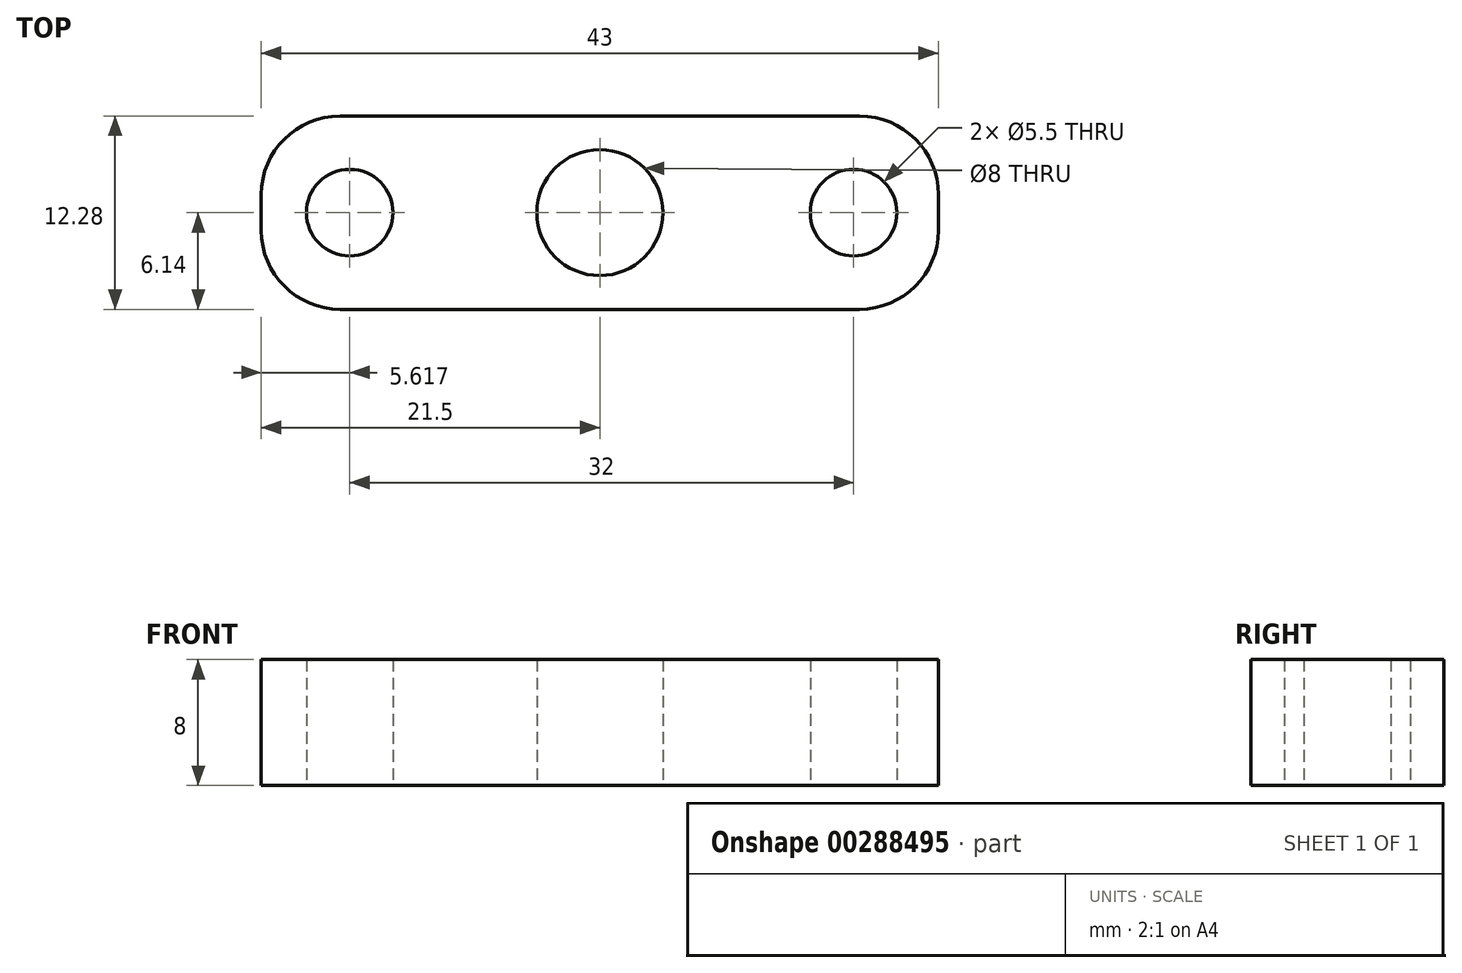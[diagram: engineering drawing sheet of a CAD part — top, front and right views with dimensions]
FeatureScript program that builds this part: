
annotation { "Feature Type Name" : "Feature", "Feature Type Description" : "" }
export const myFeature = defineFeature(function(context is Context, id is Id, definition is map)
    precondition{}
    {
        {
            var Q0;
            Q0=qCreatedBy(makeId("Top.planeOp"),FACE);
            var sketch = newSketch(context, id + "F0", { "sketchPlane" : qUnion([Q0])});
            skLineSegment(sketch, "E0.bottom", {"start": v(16.5, -6.14) * mm, "end": v(-16.5, -6.14) * mm});
            skLineSegment(sketch, "E0.top", {"start": v(16.5, 6.14) * mm, "end": v(-16.5, 6.14) * mm});
            skLineSegment(sketch, "E0.left", {"start": v(21.5, -1.14) * mm, "end": v(21.5, 1.14) * mm});
            skLineSegment(sketch, "E0.right", {"start": v(-21.5, -1.14) * mm, "end": v(-21.5, 1.14) * mm});
            skPoint(sketch, "E0.middle", {"position": v(0, 0) * mm});
            skCircle(sketch, "E1", {"center": v(0, 0) * mm, "radius": 4 * mm});
            skPoint(sketch, "E2.middle", {"position": v(0, 5.56) * mm});
            skCircle(sketch, "E3", {"center": v(-15.88, 0) * mm, "radius": 2.75 * mm});
            skCircle(sketch, "E4", {"center": v(16.12, 0) * mm, "radius": 2.75 * mm});
            skPoint(sketch, "E5.visualSharp", {"position": v(-21.5, 6.14) * mm});
            skArc(sketch, "E5.filletArc", {"start": v(-16.5, 6.14) * mm, "mid": v(-20.04, 4.67) * mm, "end": v(-21.5, 1.14) * mm});
            skPoint(sketch, "E6.visualSharp", {"position": v(-21.5, -6.14) * mm});
            skArc(sketch, "E6.filletArc", {"start": v(-21.5, -1.14) * mm, "mid": v(-20.04, -4.67) * mm, "end": v(-16.5, -6.14) * mm});
            skPoint(sketch, "E7.visualSharp", {"position": v(21.5, 6.14) * mm});
            skArc(sketch, "E7.filletArc", {"start": v(21.5, 1.14) * mm, "mid": v(20.04, 4.67) * mm, "end": v(16.5, 6.14) * mm});
            skPoint(sketch, "E8.visualSharp", {"position": v(21.5, -6.14) * mm});
            skArc(sketch, "E8.filletArc", {"start": v(16.5, -6.14) * mm, "mid": v(20.04, -4.67) * mm, "end": v(21.5, -1.14) * mm});
            skSolve(sketch);
        }
        {
            var Q0;
            Q0=makeQuery(id+"F0.imprint","IMPRINT",FACE,{"disambiguationData":[TD([[makeQuery(id+"F0.imprint","IMPRINT",EDGE,{"derivedFrom":sQuery(id+"F0.wireOp",EDGE,"E0.bottom")}),-1.0]])]});
            extrude(context, id + "F1", {"entities" : qUnion([Q0]), "depth" : 8 * mm});
        }
    });
